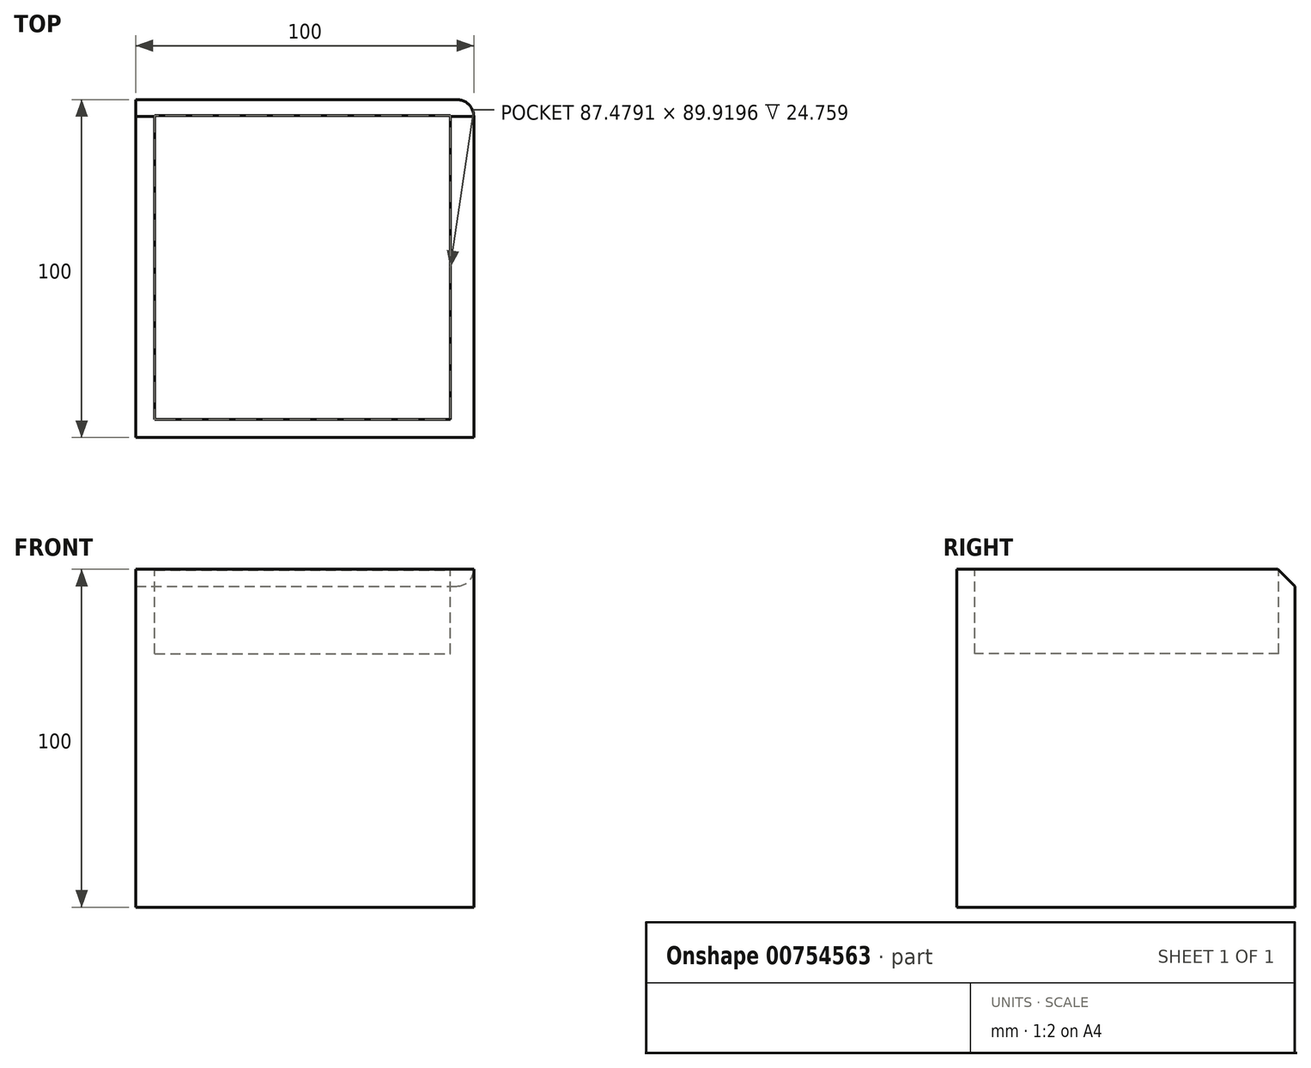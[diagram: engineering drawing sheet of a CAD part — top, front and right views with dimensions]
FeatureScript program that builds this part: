
annotation { "Feature Type Name" : "Feature", "Feature Type Description" : "" }
export const myFeature = defineFeature(function(context is Context, id is Id, definition is map)
    precondition{}
    {
        {
            var Q0;
            Q0=qCreatedBy(makeId("Top.planeOp"),FACE);
            var sketch = newSketch(context, id + "F0", { "sketchPlane" : qUnion([Q0])});
            skLineSegment(sketch, "E0.bottom", {"start": v(-50, 50) * mm, "end": v(50, 50) * mm});
            skLineSegment(sketch, "E0.top", {"start": v(-50, -50) * mm, "end": v(50, -50) * mm});
            skLineSegment(sketch, "E0.left", {"start": v(-50, 50) * mm, "end": v(-50, -50) * mm});
            skLineSegment(sketch, "E0.right", {"start": v(50, 50) * mm, "end": v(50, -50) * mm});
            skSolve(sketch);
        }
        {
            var Q0;
            Q0=makeQuery(id+"F0.imprint","IMPRINT",FACE,{"disambiguationData":[TD([[makeQuery(id+"F0.imprint","IMPRINT",EDGE,{"derivedFrom":sQuery(id+"F0.wireOp",EDGE,"E0.bottom")}),-1.0]])]});
            extrude(context, id + "F1", {"entities" : qUnion([Q0]), "depth" : 100 * mm, "offsetDistance" : 25 * mm});
        }
        {
            var Q0;
            Q0=makeQuery(id+"F1.opExtrude","CAP_FACE",FACE,{"disambiguationData":[OSD([sQuery(id+"F0.wireOp",EDGE,"E0.bottom"),sQuery(id+"F0.wireOp",EDGE,"E0.top"),sQuery(id+"F0.wireOp",EDGE,"E0.left"),sQuery(id+"F0.wireOp",EDGE,"E0.right")])],"isStart":false});
            var sketch = newSketch(context, id + "F2", { "sketchPlane" : qUnion([Q0])});
            skLineSegment(sketch, "E1.bottom", {"start": v(-44.4, 45.24) * mm, "end": v(43.08, 45.24) * mm});
            skLineSegment(sketch, "E1.top", {"start": v(-44.4, -44.68) * mm, "end": v(43.08, -44.68) * mm});
            skLineSegment(sketch, "E1.left", {"start": v(-44.4, 45.24) * mm, "end": v(-44.4, -44.68) * mm});
            skLineSegment(sketch, "E1.right", {"start": v(43.08, 45.24) * mm, "end": v(43.08, -44.68) * mm});
            skPoint(sketch, "E2.0", {"position": v(-50, -50) * mm});
            skLineSegment(sketch, "E3.0", {"start": v(-50, 50) * mm, "end": v(-50, -50) * mm});
            skSolve(sketch);
        }
        {
            var Q0;
            Q0=makeQuery(id+"F2.imprint","IMPRINT",FACE,{"disambiguationData":[TD([[makeQuery(id+"F2.imprint","IMPRINT",EDGE,{"derivedFrom":sQuery(id+"F2.wireOp",EDGE,"E1.bottom")}),-1.0]])]});
            extrude(context, id + "F3", {"entities" : qUnion([Q0]), "operationType" : NewBodyOperationType.REMOVE, "oppositeDirection" : true, "depth" : 25 * mm, "offsetDistance" : 25 * mm});
        }
        {
            var Q0;
            Q0=makeQuery(id+"F1.opExtrude","CAP_EDGE",EDGE,{"disambiguationData":[OSD([sQuery(id+"F0.wireOp",EDGE,"E0.bottom")])],"isStart":false});
            chamfer(context, id + "F4", {"entities" : qUnion([Q0]), "width" : 5 * mm, "tangentPropagation" : true});
        }
        {
            var Q0;
            Q0=makeQuery(id+"F1.opExtrude","SWEPT_EDGE",EDGE,{"disambiguationData":[OSD([sQuery(id+"F0.wireOp",EDGE,"E0.bottom"),sQuery(id+"F0.wireOp",EDGE,"E0.right")])]});
            fillet(context, id + "F5", {"entities" : qUnion([Q0]), "radius" : 5 * mm, "tangentPropagation" : true, "allowEdgeOverflow" : false});
        }
    });
